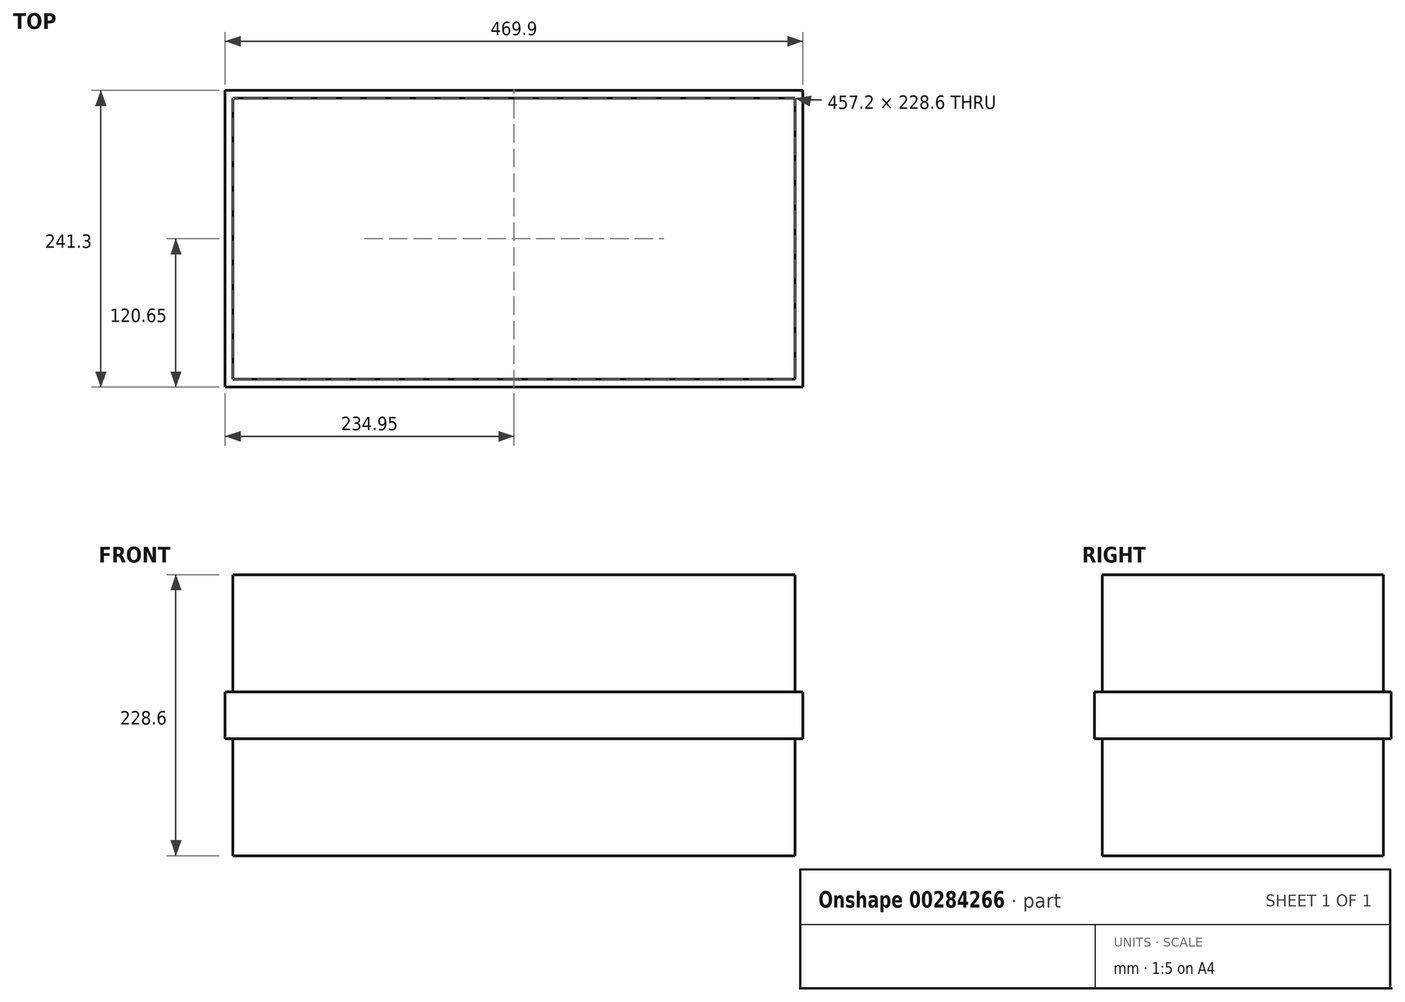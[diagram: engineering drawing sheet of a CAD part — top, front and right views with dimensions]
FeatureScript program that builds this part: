
annotation { "Feature Type Name" : "Feature", "Feature Type Description" : "" }
export const myFeature = defineFeature(function(context is Context, id is Id, definition is map)
    precondition{}
    {
        {
            var Q0;
            Q0=qCreatedBy(makeId("Top.planeOp"),FACE);
            var sketch = newSketch(context, id + "F0", { "sketchPlane" : qUnion([Q0])});
            skLineSegment(sketch, "E0.bottom", {"start": v(-228.6, -114.3) * mm, "end": v(228.6, -114.3) * mm});
            skLineSegment(sketch, "E0.top", {"start": v(-228.6, 114.3) * mm, "end": v(228.6, 114.3) * mm});
            skLineSegment(sketch, "E0.left", {"start": v(-228.6, -114.3) * mm, "end": v(-228.6, 114.3) * mm});
            skLineSegment(sketch, "E0.right", {"start": v(228.6, -114.3) * mm, "end": v(228.6, 114.3) * mm});
            skLineSegment(sketch, "E1", {"start": v(-228.6, 114.3) * mm, "end": v(228.6, -114.3) * mm, "construction": true});
            skLineSegment(sketch, "E2", {"start": v(-228.6, -114.3) * mm, "end": v(228.6, 114.3) * mm, "construction": true});
            skSolve(sketch);
        }
        {
            var Q0;
            Q0 = qSketchRegion(id + "F0", true);
            extrude(context, id + "F1", {"entities" : qUnion([Q0]), "endBound" : BoundingType.SYMMETRIC, "depth" : 228.6 * mm});
        }
        {
            var Q0;
            Q0=qCreatedBy(makeId("Top.planeOp"),FACE);
            var sketch = newSketch(context, id + "F2", { "sketchPlane" : qUnion([Q0])});
            skLineSegment(sketch, "E3.bottom", {"start": v(-234.95, 120.65) * mm, "end": v(234.95, 120.65) * mm});
            skLineSegment(sketch, "E3.top", {"start": v(-234.95, -120.65) * mm, "end": v(234.95, -120.65) * mm});
            skLineSegment(sketch, "E3.left", {"start": v(-234.95, 120.65) * mm, "end": v(-234.95, -120.65) * mm});
            skLineSegment(sketch, "E3.right", {"start": v(234.95, 120.65) * mm, "end": v(234.95, -120.65) * mm});
            skLineSegment(sketch, "E4", {"start": v(0, 120.65) * mm, "end": v(0, 114.3) * mm, "construction": true});
            skLineSegment(sketch, "E5", {"start": v(-228.6, 0) * mm, "end": v(-234.95, 0) * mm, "construction": true});
            skLineSegment(sketch, "E6", {"start": v(0, -114.3) * mm, "end": v(0, -120.65) * mm, "construction": true});
            skLineSegment(sketch, "E7", {"start": v(228.6, 0) * mm, "end": v(234.95, 0) * mm, "construction": true});
            skSolve(sketch);
        }
        {
            var Q0;
            Q0 = qSketchRegion(id + "F2", true);
            extrude(context, id + "F3", {"entities" : qUnion([Q0]), "operationType" : NewBodyOperationType.ADD, "endBound" : BoundingType.SYMMETRIC, "depth" : 38.1 * mm});
        }
    });
